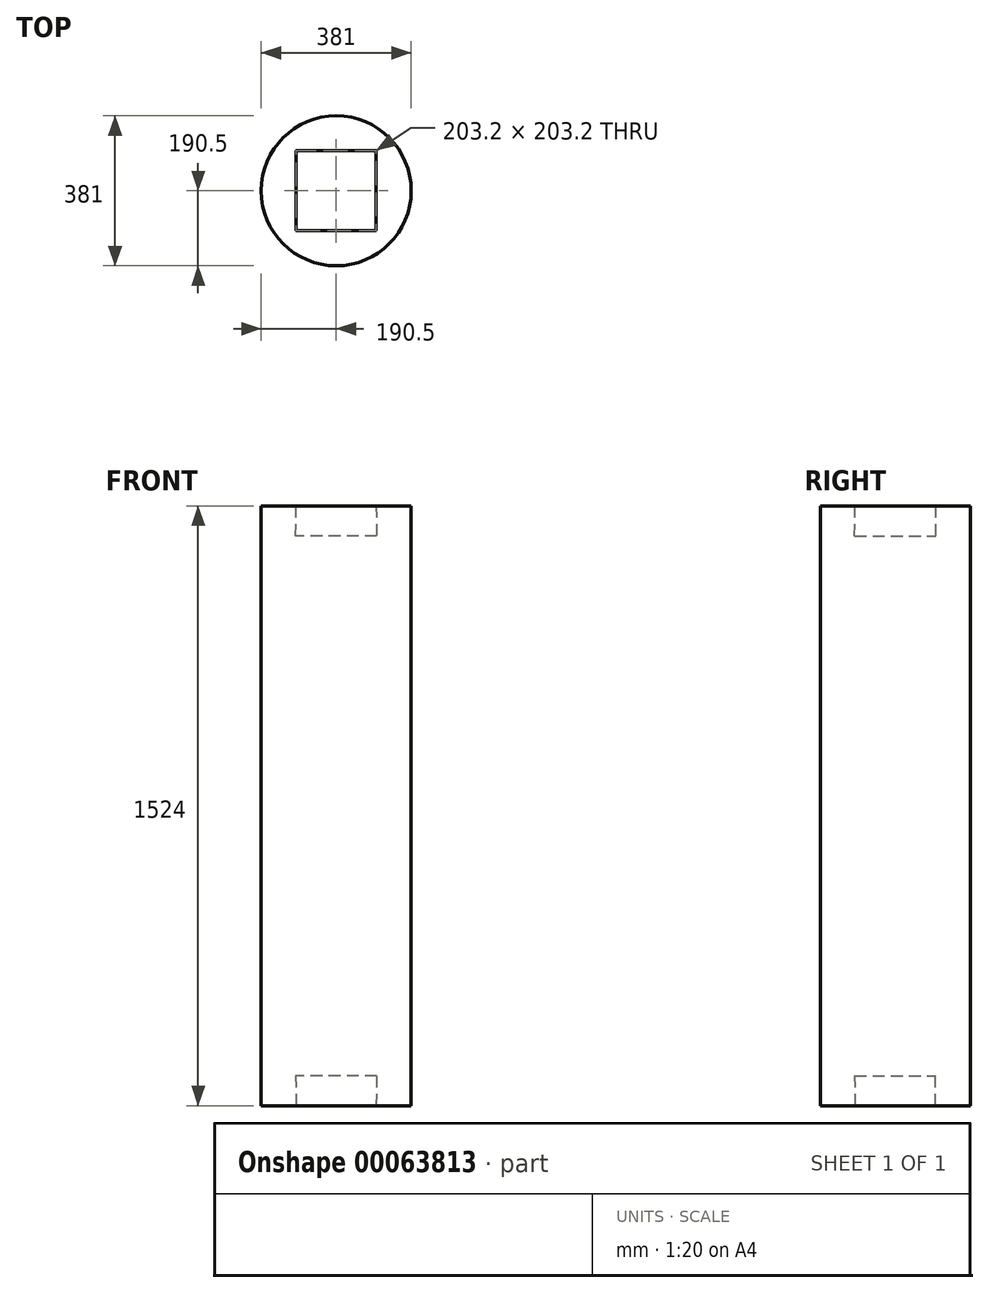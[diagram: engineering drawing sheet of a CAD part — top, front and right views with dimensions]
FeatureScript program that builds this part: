
annotation { "Feature Type Name" : "Feature", "Feature Type Description" : "" }
export const myFeature = defineFeature(function(context is Context, id is Id, definition is map)
    precondition{}
    {
        {
            var Q0;
            Q0=qCreatedBy(makeId("Top.planeOp"),FACE);
            var sketch = newSketch(context, id + "F0", { "sketchPlane" : qUnion([Q0])});
            skCircle(sketch, "E0", {"center": v(0, 0) * mm, "radius": 190.5 * mm});
            skSolve(sketch);
        }
        {
            var Q0;
            Q0=makeQuery(id+"F0.imprint","IMPRINT",FACE,{"disambiguationData":[TD([[makeQuery(id+"F0.imprint","IMPRINT",EDGE,{"derivedFrom":sQuery(id+"F0.wireOp",EDGE,"E0")}),1.0]])]});
            extrude(context, id + "F1", {"entities" : qUnion([Q0]), "depth" : 762 * mm});
        }
        {
            var Q0;
            Q0=makeQuery(id+"F1.opExtrude","CAP_FACE",FACE,{"disambiguationData":[OSD([sQuery(id+"F0.wireOp",EDGE,"E0")])],"isStart":false});
            var sketch = newSketch(context, id + "F2", { "sketchPlane" : qUnion([Q0])});
            skLineSegment(sketch, "E1.bottom", {"start": v(101.6, 101.6) * mm, "end": v(-101.6, 101.6) * mm});
            skLineSegment(sketch, "E1.top", {"start": v(101.6, -101.6) * mm, "end": v(-101.6, -101.6) * mm});
            skLineSegment(sketch, "E1.left", {"start": v(101.6, 101.6) * mm, "end": v(101.6, -101.6) * mm});
            skLineSegment(sketch, "E1.right", {"start": v(-101.6, 101.6) * mm, "end": v(-101.6, -101.6) * mm});
            skLineSegment(sketch, "E2", {"start": v(-101.6, 101.6) * mm, "end": v(101.6, -101.6) * mm, "construction": true});
            skLineSegment(sketch, "E3", {"start": v(-101.6, -101.6) * mm, "end": v(101.6, 101.6) * mm, "construction": true});
            skSolve(sketch);
        }
        {
            var Q0;
            Q0=makeQuery(id+"F2.imprint","IMPRINT",FACE,{"disambiguationData":[TD([[makeQuery(id+"F2.imprint","IMPRINT",EDGE,{"derivedFrom":sQuery(id+"F2.wireOp",EDGE,"E1.bottom")}),1.0]])]});
            extrude(context, id + "F3", {"entities" : qUnion([Q0]), "operationType" : NewBodyOperationType.REMOVE, "oppositeDirection" : true, "depth" : 76.2 * mm, "hasDraft" : true, "draftAngle" : 1 * degree});
        }
        {
            var Q0;
            Q0=makeQuery(id+"F1.opExtrude","SWEPT_BODY",BODY,{"disambiguationData":[OSD([sQuery(id+"F0.wireOp",EDGE,"E0")])]});
            var Q1;
            Q1=makeQuery(id+"F1.opExtrude","CAP_FACE",FACE,{"disambiguationData":[OSD([sQuery(id+"F0.wireOp",EDGE,"E0")])],"isStart":true});
            mirror(context, id + "F4", {"operationType" : NewBodyOperationType.ADD, "entities" : qUnion([Q0]), "mirrorPlane" : qUnion([Q1])});
        }
    });
